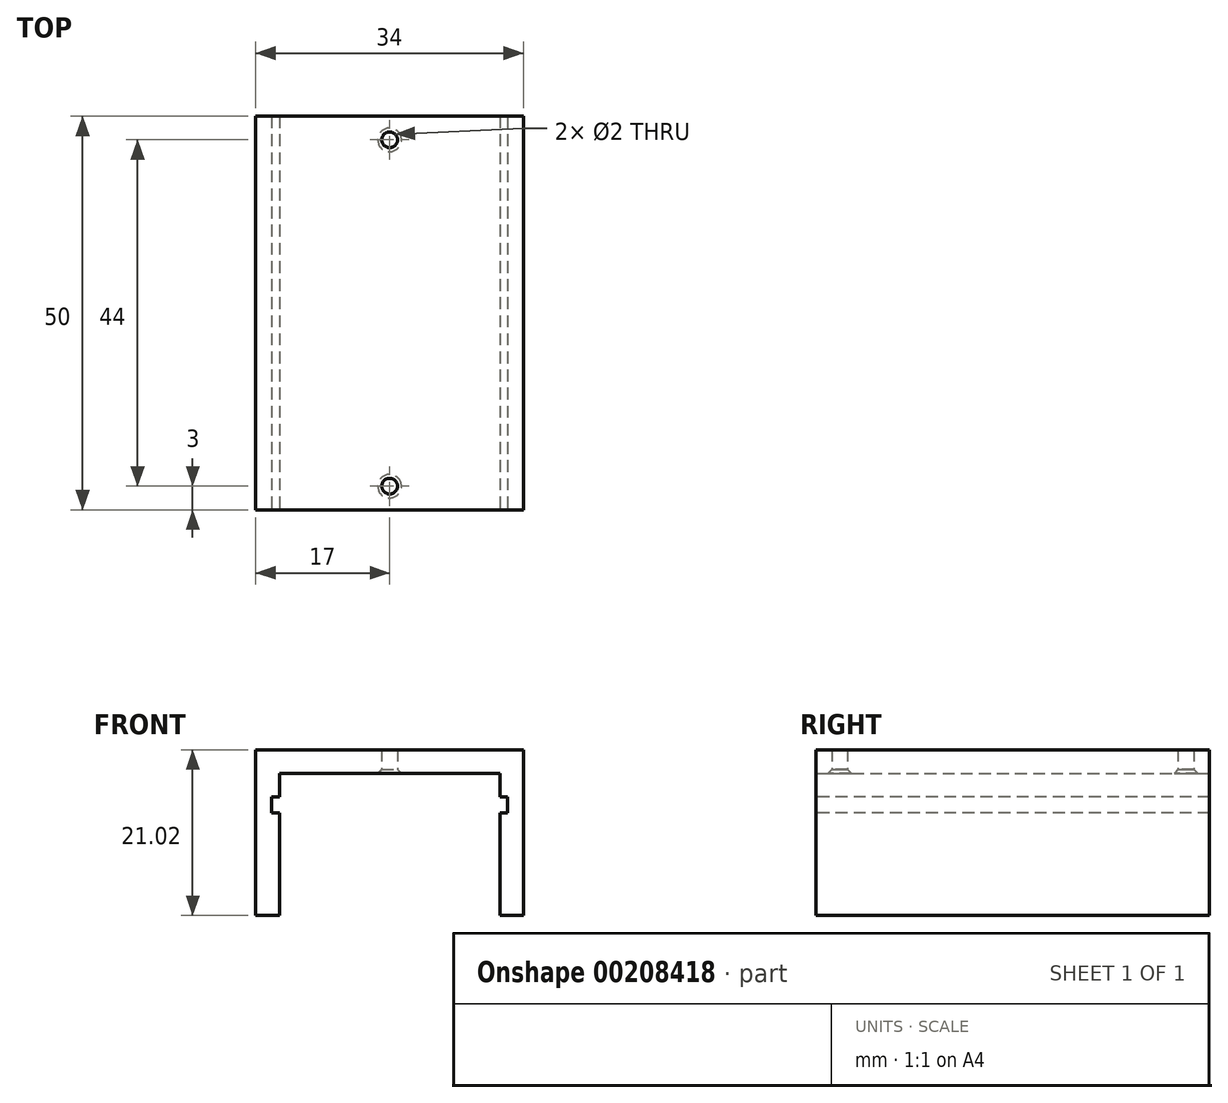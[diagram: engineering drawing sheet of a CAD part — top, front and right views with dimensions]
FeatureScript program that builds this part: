
annotation { "Feature Type Name" : "Feature", "Feature Type Description" : "" }
export const myFeature = defineFeature(function(context is Context, id is Id, definition is map)
    precondition{}
    {
        {
            var Q0;
            Q0=qCreatedBy(makeId("Front.planeOp"),FACE);
            var sketch = newSketch(context, id + "F0", { "sketchPlane" : qUnion([Q0])});
            skLineSegment(sketch, "E0.bottom", {"start": v(0, 0) * mm, "end": v(-3, 0) * mm});
            skLineSegment(sketch, "E0.top", {"start": v(0, -21) * mm, "end": v(-3, -21) * mm});
            skLineSegment(sketch, "E0.left", {"start": v(0, 0) * mm, "end": v(0, -21) * mm});
            skLineSegment(sketch, "E0.right", {"start": v(-3, 0) * mm, "end": v(-3, -21) * mm});
            skLineSegment(sketch, "E1.bottom", {"start": v(0, 0) * mm, "end": v(28, 0) * mm});
            skLineSegment(sketch, "E1.top", {"start": v(0, -3) * mm, "end": v(28, -3) * mm});
            skLineSegment(sketch, "E1.left", {"start": v(0, 0) * mm, "end": v(0, -3) * mm});
            skLineSegment(sketch, "E1.right", {"start": v(28, 0) * mm, "end": v(28, -3) * mm});
            skLineSegment(sketch, "E2.bottom", {"start": v(28, 0) * mm, "end": v(31, 0) * mm});
            skLineSegment(sketch, "E2.top", {"start": v(28, -21.02) * mm, "end": v(31, -21.02) * mm});
            skLineSegment(sketch, "E2.left", {"start": v(28, 0) * mm, "end": v(28, -21.02) * mm});
            skLineSegment(sketch, "E2.right", {"start": v(31, 0) * mm, "end": v(31, -21.02) * mm});
            skSolve(sketch);
        }
        {
            var Q0;
            Q0=makeQuery(id+"F0.imprint","IMPRINT",FACE,{"disambiguationData":[TD([[makeQuery(id+"F0.imprint","IMPRINT",EDGE,{"derivedFrom":sQuery(id+"F0.wireOp",EDGE,"E0.bottom")}),1.0]])]});
            var Q1;
            {var subQ0=sQuery(id+"F0.wireOp",EDGE,"E1.bottom");Q1=makeQuery(id+"F0.imprint","IMPRINT",FACE,{"disambiguationData":[TD([[makeQuery(id+"F0.imprint","IMPRINT",EDGE,{"derivedFrom":subQ0}),-1.0]])]});}
            var Q2;
            {var subQ3=sQuery(id+"F0.wireOp",EDGE,"E2.bottom");Q2=makeQuery(id+"F0.imprint","IMPRINT",FACE,{"disambiguationData":[TD([[makeQuery(id+"F0.imprint","IMPRINT",EDGE,{"derivedFrom":subQ3}),-1.0]])]});}
            extrude(context, id + "F1", {"entities" : qUnion([Q0, Q1, Q2]), "depth" : 50 * mm});
        }
        {
            var Q0;
            Q0=makeQuery(id+"F1.opExtrude","CAP_FACE",FACE,{"disambiguationData":[OSD([sQuery(id+"F0.wireOp",EDGE,"E0.bottom"),sQuery(id+"F0.wireOp",EDGE,"E0.top"),sQuery(id+"F0.wireOp",EDGE,"E0.left"),sQuery(id+"F0.wireOp",EDGE,"E0.right"),sQuery(id+"F0.wireOp",EDGE,"E1.bottom"),sQuery(id+"F0.wireOp",EDGE,"E1.top"),sQuery(id+"F0.wireOp",EDGE,"E2.bottom"),sQuery(id+"F0.wireOp",EDGE,"E2.top"),sQuery(id+"F0.wireOp",EDGE,"E2.left"),sQuery(id+"F0.wireOp",EDGE,"E2.right")])],"isStart":false});
            var sketch = newSketch(context, id + "F2", { "sketchPlane" : qUnion([Q0])});
            skLineSegment(sketch, "E3.bottom", {"start": v(0, -6) * mm, "end": v(-1, -6) * mm});
            skLineSegment(sketch, "E3.top", {"start": v(0, -8) * mm, "end": v(-1, -8) * mm});
            skLineSegment(sketch, "E3.left", {"start": v(0, -6) * mm, "end": v(0, -8) * mm});
            skLineSegment(sketch, "E3.right", {"start": v(-1, -6) * mm, "end": v(-1, -8) * mm});
            skLineSegment(sketch, "E4", {"start": v(14, -3) * mm, "end": v(14, -24.24) * mm});
            skLineSegment(sketch, "E5.MirrorCS", {"start": v(28, -6) * mm, "end": v(29, -6) * mm});
            skLineSegment(sketch, "E6.MirrorCS", {"start": v(28, -6) * mm, "end": v(28, -8) * mm});
            skLineSegment(sketch, "E7.MirrorCS", {"start": v(29, -6) * mm, "end": v(29, -8) * mm});
            skLineSegment(sketch, "E8.MirrorCS", {"start": v(28, -8) * mm, "end": v(29, -8) * mm});
            skSolve(sketch);
        }
        {
            var Q0;
            Q0=makeQuery(id+"F2.imprint","IMPRINT",FACE,{"disambiguationData":[TD([[makeQuery(id+"F2.imprint","IMPRINT",EDGE,{"derivedFrom":sQuery(id+"F2.wireOp",EDGE,"E3.bottom")}),1.0]])]});
            var Q1;
            Q1=makeQuery(id+"F2.imprint","IMPRINT",FACE,{"disambiguationData":[TD([[makeQuery(id+"F2.imprint","IMPRINT",EDGE,{"derivedFrom":sQuery(id+"F2.wireOp",EDGE,"E5.MirrorCS")}),-1.0]])]});
            extrude(context, id + "F3", {"entities" : qUnion([Q0, Q1]), "operationType" : NewBodyOperationType.REMOVE, "oppositeDirection" : true, "depth" : 50 * mm});
        }
        {
            var Q0;
            Q0=makeQuery(id+"F1.opExtrude","SWEPT_FACE",FACE,{"disambiguationData":[OSD([sQuery(id+"F0.wireOp",EDGE,"E1.top")])]});
            var sketch = newSketch(context, id + "F4", { "sketchPlane" : qUnion([Q0])});
            skLineSegment(sketch, "E9", {"start": v(14, 50) * mm, "end": v(14, 47) * mm});
            skPoint(sketch, "E9.endSnap0", {"position": v(14, 50) * mm});
            skPoint(sketch, "E10", {"position": v(14, 47) * mm});
            skLineSegment(sketch, "E11", {"start": v(0, 25) * mm, "end": v(52.37, 25) * mm});
            skPoint(sketch, "E11.endSnap0", {"position": v(0, 25) * mm});
            skPoint(sketch, "E12.MirrorP", {"position": v(14, 3) * mm});
            skSolve(sketch);
        }
        {
            var Q0;
            Q0=sQuery(id+"F4.wireOp",VERTEX,"E10");
            var Q1;
            Q1=makeQuery(id+"F1.opExtrude","SWEPT_BODY",BODY,{"disambiguationData":[OSD([sQuery(id+"F0.wireOp",EDGE,"E0.bottom"),sQuery(id+"F0.wireOp",EDGE,"E0.top"),sQuery(id+"F0.wireOp",EDGE,"E0.left"),sQuery(id+"F0.wireOp",EDGE,"E0.right"),sQuery(id+"F0.wireOp",EDGE,"E1.bottom"),sQuery(id+"F0.wireOp",EDGE,"E1.top"),sQuery(id+"F0.wireOp",EDGE,"E2.bottom"),sQuery(id+"F0.wireOp",EDGE,"E2.top"),sQuery(id+"F0.wireOp",EDGE,"E2.left"),sQuery(id+"F0.wireOp",EDGE,"E2.right")])]});
            hole(context, id + "F5", {"style" : HoleStyle.C_SINK, "endStyle" : HoleEndStyle.THROUGH, "holeDiameter" : 2 * mm, "cSinkDiameter" : 3 * mm, "cSinkAngle" : 90 * degree, "locations" : qUnion([Q0]), "scope" : qUnion([Q1]), "isTappedThrough" : true});
        }
        {
            var Q0;
            Q0=sQuery(id+"F4.wireOp",VERTEX,"E12.MirrorP");
            var Q1;
            Q1=makeQuery(id+"F1.opExtrude","SWEPT_BODY",BODY,{"disambiguationData":[OSD([sQuery(id+"F0.wireOp",EDGE,"E0.bottom"),sQuery(id+"F0.wireOp",EDGE,"E0.top"),sQuery(id+"F0.wireOp",EDGE,"E0.left"),sQuery(id+"F0.wireOp",EDGE,"E0.right"),sQuery(id+"F0.wireOp",EDGE,"E1.bottom"),sQuery(id+"F0.wireOp",EDGE,"E1.top"),sQuery(id+"F0.wireOp",EDGE,"E2.bottom"),sQuery(id+"F0.wireOp",EDGE,"E2.top"),sQuery(id+"F0.wireOp",EDGE,"E2.left"),sQuery(id+"F0.wireOp",EDGE,"E2.right")])]});
            hole(context, id + "F6", {"style" : HoleStyle.C_SINK, "endStyle" : HoleEndStyle.THROUGH, "holeDiameter" : 2 * mm, "cSinkDiameter" : 3 * mm, "cSinkAngle" : 90 * degree, "locations" : qUnion([Q0]), "scope" : qUnion([Q1]), "isTappedThrough" : true});
        }
    });
